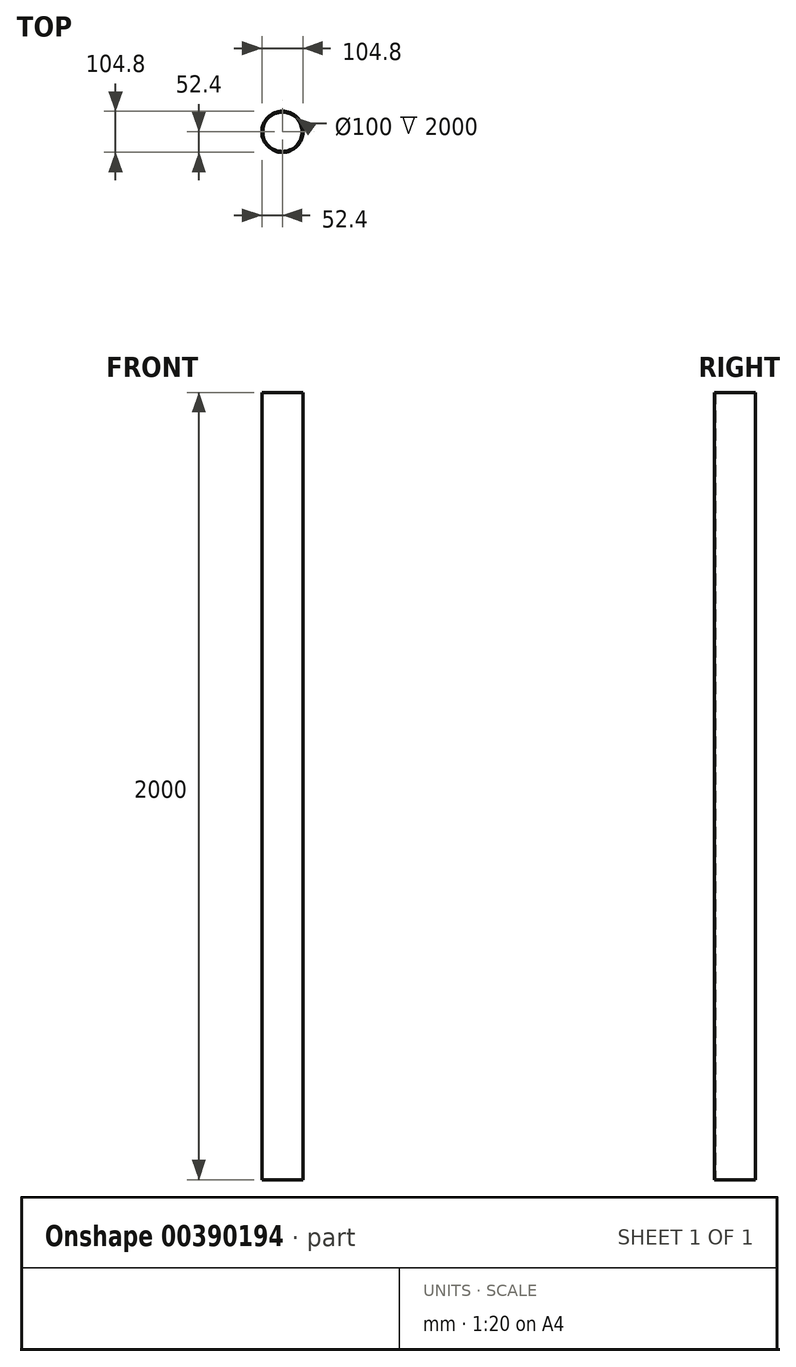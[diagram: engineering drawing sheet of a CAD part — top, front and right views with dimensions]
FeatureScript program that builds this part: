
annotation { "Feature Type Name" : "Feature", "Feature Type Description" : "" }
export const myFeature = defineFeature(function(context is Context, id is Id, definition is map)
    precondition{}
    {
        {
            var Q0;
            Q0=qCreatedBy(makeId("Top.planeOp"),FACE);
            var sketch = newSketch(context, id + "F0", { "sketchPlane" : qUnion([Q0])});
            skCircle(sketch, "E0", {"center": v(0, 0) * mm, "radius": 50 * mm});
            skCircle(sketch, "E1", {"center": v(0, 0) * mm, "radius": 52.4 * mm});
            skSolve(sketch);
        }
        {
            var Q0;
            Q0=makeQuery(id+"F0.imprint","IMPRINT",FACE,{"disambiguationData":[TD([[makeQuery(id+"F0.imprint","IMPRINT",EDGE,{"derivedFrom":sQuery(id+"F0.wireOp",EDGE,"E0")}),-1.0]])]});
            extrude(context, id + "F1", {"entities" : qUnion([Q0]), "depth" : 2000 * mm});
        }
    });
